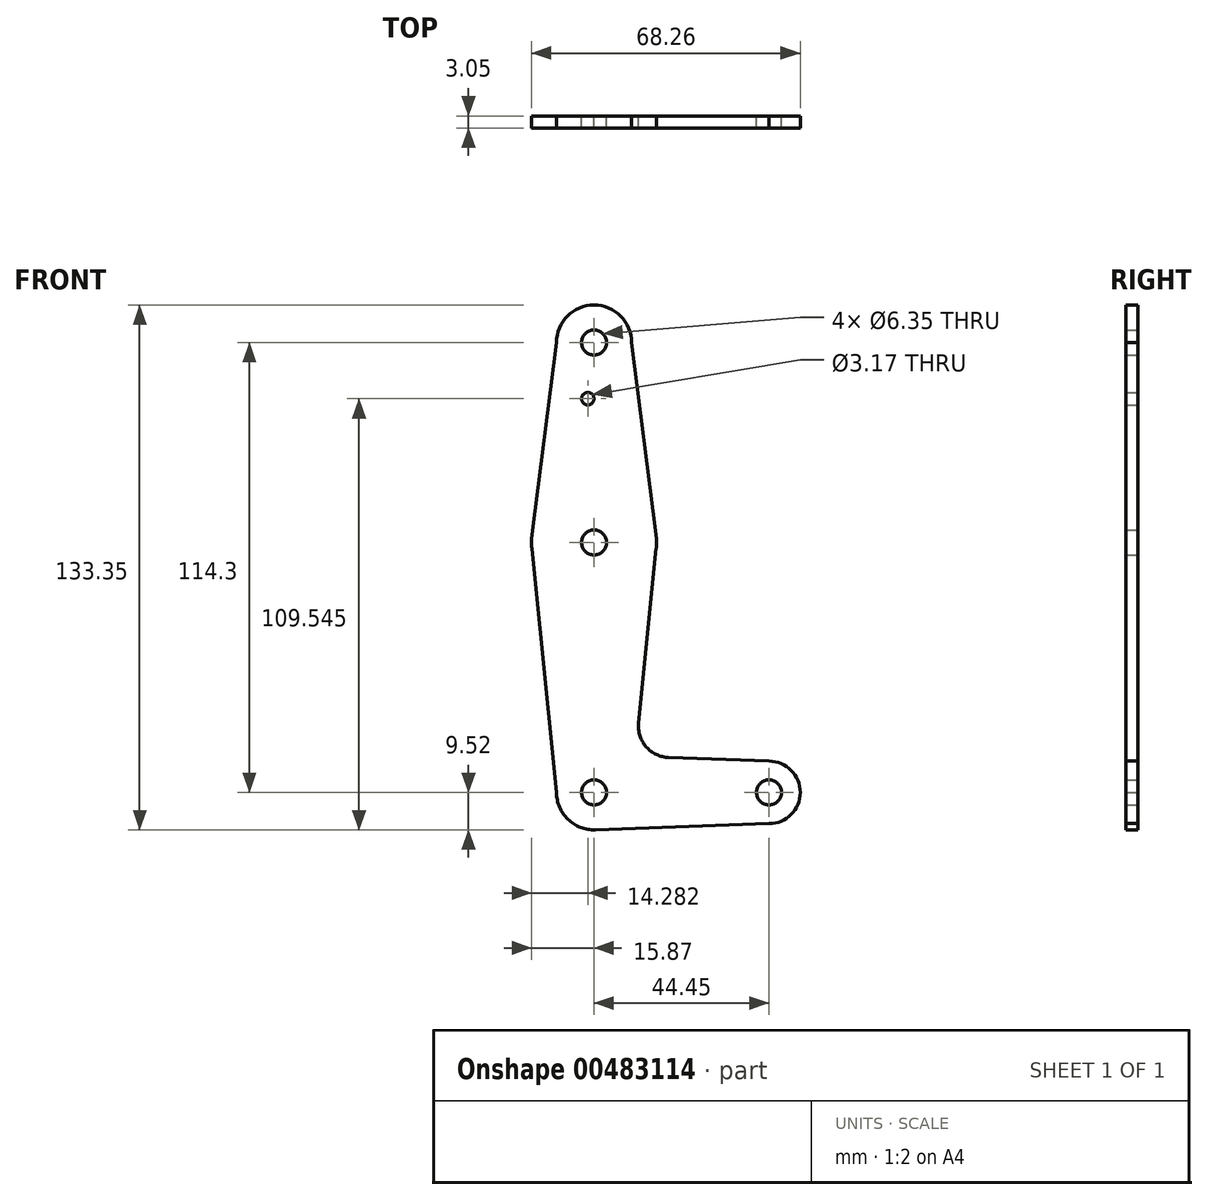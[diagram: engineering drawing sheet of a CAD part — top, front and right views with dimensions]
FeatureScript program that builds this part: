
annotation { "Feature Type Name" : "Feature", "Feature Type Description" : "" }
export const myFeature = defineFeature(function(context is Context, id is Id, definition is map)
    precondition{}
    {
        {
            var Q0;
            Q0=qCreatedBy(makeId("Front.planeOp"),FACE);
            var sketch = newSketch(context, id + "F0", { "sketchPlane" : qUnion([Q0])});
            skLineSegment(sketch, "E0", {"start": v(0, 0) * mm, "end": v(44.45, 0) * mm, "construction": true});
            skLineSegment(sketch, "E1", {"start": v(0, 0) * mm, "end": v(0, 114.3) * mm, "construction": true});
            skCircle(sketch, "E2", {"center": v(0, 114.3) * mm, "radius": 9.53 * mm});
            skCircle(sketch, "E3", {"center": v(0, 63.5) * mm, "radius": 15.88 * mm});
            skCircle(sketch, "E4", {"center": v(0, 0) * mm, "radius": 9.53 * mm});
            skCircle(sketch, "E5", {"center": v(44.45, 0) * mm, "radius": 7.94 * mm});
            skLineSegment(sketch, "E6", {"start": v(-9.52, 0) * mm, "end": v(-15.8, 61.9) * mm});
            skLineSegment(sketch, "E7", {"start": v(-9.53, 114.3) * mm, "end": v(-15.75, 65.5) * mm});
            skLineSegment(sketch, "E8", {"start": v(9.52, 114.3) * mm, "end": v(15.75, 65.5) * mm});
            skLineSegment(sketch, "E9", {"start": v(44.45, 7.94) * mm, "end": v(18.97, 8.85) * mm});
            skLineSegment(sketch, "E10", {"start": v(44.45, -7.94) * mm, "end": v(0, -9.53) * mm});
            skCircle(sketch, "E11", {"center": v(0, 114.3) * mm, "radius": 3.18 * mm});
            skCircle(sketch, "E12", {"center": v(0, 63.5) * mm, "radius": 3.18 * mm});
            skCircle(sketch, "E13", {"center": v(0, 0) * mm, "radius": 3.18 * mm});
            skCircle(sketch, "E14", {"center": v(44.45, 0) * mm, "radius": 3.18 * mm});
            skCircle(sketch, "E15", {"center": v(-1.59, 100.03) * mm, "radius": 1.59 * mm});
            skLineSegment(sketch, "E16", {"start": v(15.8, 61.91) * mm, "end": v(11.34, 17.6) * mm});
            skArc(sketch, "E17.filletArc", {"start": v(11.34, 17.6) * mm, "mid": v(13.26, 11.57) * mm, "end": v(18.97, 8.85) * mm});
            skSolve(sketch);
        }
        {
            var Q0;
            Q0 = qSketchRegion(id + "F0", true);
            extrude(context, id + "F1", {"entities" : qUnion([Q0]), "depth" : 3.05 * mm});
        }
    });
